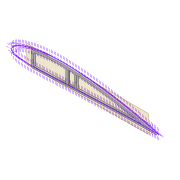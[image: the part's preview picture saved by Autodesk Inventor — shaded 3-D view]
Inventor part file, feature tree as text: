
AUTODESK INVENTOR PART (.ipt)
format: ipt  version: 2022 (Build 260153000, 153)  size: 322,560 bytes
history: native  units: mm
features: extrude x5, sketch x5, projected_geometry x4, shell x1, fillet x1, plane x1
ambient origin geometry x8: Origin, YZ Plane, XZ Plane, XY Plane, X Axis, Y Axis, Z Axis, Center Point
bodies: Solid1 (feature_tree)
feature tree (17):
  extrude  "Extrusion1"  Depth=5.0mm
  shell  "Shell1"  Thickness=2.0mm
  extrude  "Extrusion8"  Depth=5.9mm
  extrude  "Extrusion3"  Depth=10.0mm TaperAngle=0.0deg
  extrude  "Extrusion4"  Depth=5.0mm
  fillet  "Fillet1"  Radius=5.0mm
  extrude  "Extrusion5"  Depth=5.0mm
  plane  "Work Plane2"
  sketch  "Sketch3"  dims[d0=4.0mm d1=0.0mm d2=5.0mm d7=2.0mm]
  sketch  "Sketch8"  dims[d8=2.0mm d9=5.9mm]
  sketch  "Sketch9"  dims[d13=10.0mm d14=0.0mm d16=10.0mm d17=0.0mm]
  sketch  "Sketch10"  dims[d22=4.0mm d23=0.0mm d31=2.0mm d32=5.0mm]
  projected_geometry  "Projected Loop4"
  projected_geometry  "Projected Loop10"
  sketch  "Sketch24"  dims[d33=130.0mm d34=1.6mm d35=2.5mm d36=12.0mm d37=5.0mm d38=1.6mm d39=150.0mm d40=2.5mm d62=50.0mm d63=6.0mm d64=4.0mm d65=0.0mm d66=3.0mm d67=6.0mm]
  projected_geometry  "Projected Loop11"
  projected_geometry  "Projected Loop12"
